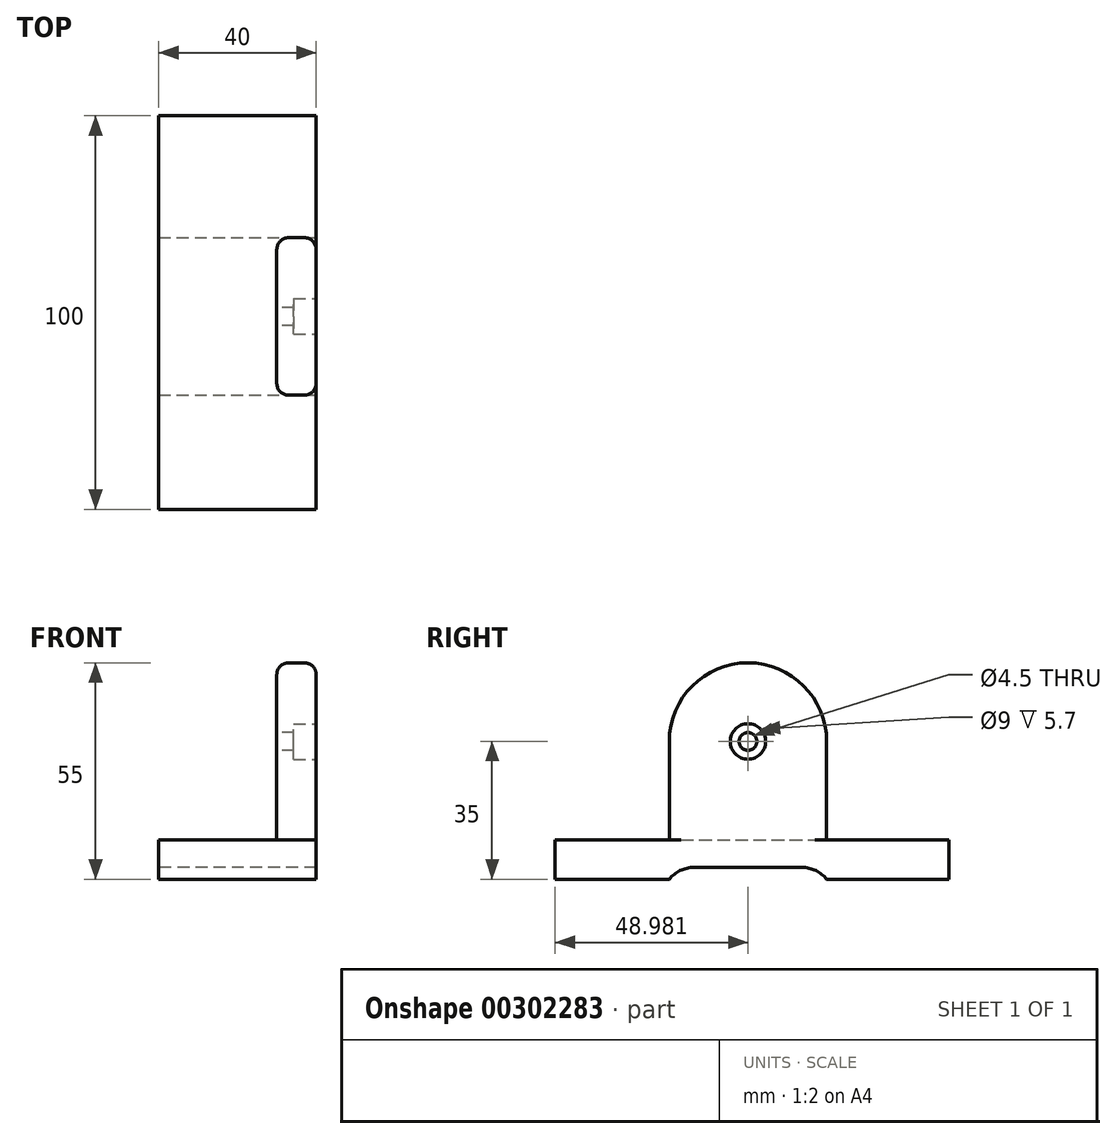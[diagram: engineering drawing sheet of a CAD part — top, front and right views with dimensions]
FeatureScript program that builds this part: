
annotation { "Feature Type Name" : "Feature", "Feature Type Description" : "" }
export const myFeature = defineFeature(function(context is Context, id is Id, definition is map)
    precondition{}
    {
        {
            var Q0;
            Q0=qCreatedBy(makeId("Top.planeOp"),FACE);
            var sketch = newSketch(context, id + "F0", { "sketchPlane" : qUnion([Q0])});
            skLineSegment(sketch, "E0.bottom", {"start": v(0, 0) * mm, "end": v(40, 0) * mm});
            skLineSegment(sketch, "E0.top", {"start": v(0, 100) * mm, "end": v(40, 100) * mm});
            skLineSegment(sketch, "E0.left", {"start": v(0, 0) * mm, "end": v(0, 100) * mm});
            skLineSegment(sketch, "E0.right", {"start": v(40, 0) * mm, "end": v(40, 100) * mm});
            skLineSegment(sketch, "E1.bottom", {"start": v(40.46, 100) * mm, "end": v(40, 100) * mm});
            skLineSegment(sketch, "E1.top", {"start": v(40.46, 96.76) * mm, "end": v(40, 96.76) * mm});
            skLineSegment(sketch, "E1.right", {"start": v(40, 100) * mm, "end": v(40, 96.76) * mm});
            skSolve(sketch);
        }
        {
            var Q0;
            Q0 = qSketchRegion(id + "F0", true);
            extrude(context, id + "F1", {"entities" : qUnion([Q0]), "depth" : 10 * mm});
        }
        {
            var Q0;
            Q0=makeQuery(id+"F1.opExtrude","SWEPT_FACE",FACE,{"disambiguationData":[OSD([sQuery(id+"F0.wireOp",EDGE,"E0.right"),sQuery(id+"F0.wireOp",EDGE,"E1.right")])]});
            var sketch = newSketch(context, id + "F2", { "sketchPlane" : qUnion([Q0])});
            skLineSegment(sketch, "E2", {"start": v(28.98, 0) * mm, "end": v(28.98, 35) * mm});
            skArc(sketch, "E3", {"start": v(28.98, 35) * mm, "mid": v(48.98, 55) * mm, "end": v(68.98, 35) * mm});
            skLineSegment(sketch, "E4", {"start": v(68.98, 35) * mm, "end": v(68.98, 0) * mm});
            skLineSegment(sketch, "E5", {"start": v(68.98, 0) * mm, "end": v(28.98, 0) * mm});
            skSolve(sketch);
        }
        {
            var Q0;
            Q0 = qSketchRegion(id + "F2", true);
            extrude(context, id + "F3", {"entities" : qUnion([Q0]), "operationType" : NewBodyOperationType.ADD, "oppositeDirection" : true, "depth" : 10 * mm});
        }
        {
            var Q0;
            Q0=makeQuery(id+"F3.opExtrude","CAP_FACE",FACE,{"disambiguationData":[OSD([sQuery(id+"F2.wireOp",EDGE,"E2"),sQuery(id+"F2.wireOp",EDGE,"E3"),sQuery(id+"F2.wireOp",EDGE,"E4"),sQuery(id+"F2.wireOp",EDGE,"E5")])],"isStart":false});
            var sketch = newSketch(context, id + "F4", { "sketchPlane" : qUnion([Q0])});
            skCircle(sketch, "E6", {"center": v(-48.98, 35) * mm, "radius": 2.25 * mm});
            skSolve(sketch);
        }
        {
            var Q0;
            Q0 = qSketchRegion(id + "F4", true);
            extrude(context, id + "F5", {"entities" : qUnion([Q0]), "operationType" : NewBodyOperationType.REMOVE, "endBound" : BoundingType.THROUGH_ALL, "oppositeDirection" : true, "depth" : 25 * mm});
        }
        {
            var Q0;
            Q0=makeQuery(id+"F3.boolean.opBoolean","MERGE",FACE,{"derivedFrom":[makeQuery(id+"F1.opExtrude","SWEPT_FACE",FACE,{"disambiguationData":[OSD([sQuery(id+"F0.wireOp",EDGE,"E0.right"),sQuery(id+"F0.wireOp",EDGE,"E1.right")])]}),makeQuery(id+"F3.opExtrude","CAP_FACE",FACE,{"disambiguationData":[OSD([sQuery(id+"F2.wireOp",EDGE,"E2"),sQuery(id+"F2.wireOp",EDGE,"E3"),sQuery(id+"F2.wireOp",EDGE,"E4"),sQuery(id+"F2.wireOp",EDGE,"E5")])],"isStart":true})]});
            var sketch = newSketch(context, id + "F6", { "sketchPlane" : qUnion([Q0])});
            skLineSegment(sketch, "E7.bottom", {"start": v(28.98, 0) * mm, "end": v(68.98, 0) * mm});
            skLineSegment(sketch, "E7.top", {"start": v(28.98, 3) * mm, "end": v(68.98, 3) * mm});
            skLineSegment(sketch, "E7.left", {"start": v(28.98, 0) * mm, "end": v(28.98, 3) * mm});
            skLineSegment(sketch, "E7.right", {"start": v(68.98, 0) * mm, "end": v(68.98, 3) * mm});
            skSolve(sketch);
        }
        {
            var Q0;
            Q0 = qSketchRegion(id + "F6", true);
            extrude(context, id + "F7", {"entities" : qUnion([Q0]), "operationType" : NewBodyOperationType.REMOVE, "endBound" : BoundingType.THROUGH_ALL, "oppositeDirection" : true, "depth" : 25 * mm});
        }
        {
            var Q0;
            Q0=makeQuery(id+"F3.boolean.opBoolean","MERGE",FACE,{"derivedFrom":[makeQuery(id+"F1.opExtrude","SWEPT_FACE",FACE,{"disambiguationData":[OSD([sQuery(id+"F0.wireOp",EDGE,"E0.right"),sQuery(id+"F0.wireOp",EDGE,"E1.right")])]}),makeQuery(id+"F3.opExtrude","CAP_FACE",FACE,{"disambiguationData":[OSD([sQuery(id+"F2.wireOp",EDGE,"E2"),sQuery(id+"F2.wireOp",EDGE,"E3"),sQuery(id+"F2.wireOp",EDGE,"E4"),sQuery(id+"F2.wireOp",EDGE,"E5")])],"isStart":true})]});
            var sketch = newSketch(context, id + "F8", { "sketchPlane" : qUnion([Q0])});
            skCircle(sketch, "E8", {"center": v(48.98, 35) * mm, "radius": 4.5 * mm});
            skSolve(sketch);
        }
        {
            var Q0;
            Q0 = qSketchRegion(id + "F8", true);
            extrude(context, id + "F9", {"entities" : qUnion([Q0]), "operationType" : NewBodyOperationType.REMOVE, "oppositeDirection" : true, "depth" : 5.7 * mm});
        }
        {
            var Q0;
            Q0=makeQuery(id+"F7.boolean.opBoolean","COPY",EDGE,{"derivedFrom":makeQuery(id+"F7.opExtrude","SWEPT_EDGE",EDGE,{"disambiguationData":[OSD([sQuery(id+"F6.wireOp",EDGE,"E7.top"),sQuery(id+"F6.wireOp",EDGE,"E7.right")])]})});
            var Q1;
            Q1=makeQuery(id+"F7.boolean.opBoolean","COPY",EDGE,{"derivedFrom":makeQuery(id+"F7.opExtrude","SWEPT_EDGE",EDGE,{"disambiguationData":[OSD([sQuery(id+"F6.wireOp",EDGE,"E7.top"),sQuery(id+"F6.wireOp",EDGE,"E7.left")])]})});
            fillet(context, id + "F10", {"entities" : qUnion([Q0, Q1]), "radius" : 8 * mm, "tangentPropagation" : true, "allowEdgeOverflow" : false});
        }
        {
            var Q0;
            Q0=makeQuery(id+"F3.opExtrude","CAP_EDGE",EDGE,{"disambiguationData":[OSD([sQuery(id+"F2.wireOp",EDGE,"E4")])],"isStart":true});
            var Q1;
            Q1=makeQuery(id+"F3.opExtrude","CAP_EDGE",EDGE,{"disambiguationData":[OSD([sQuery(id+"F2.wireOp",EDGE,"E4")])],"isStart":false});
            fillet(context, id + "F11", {"entities" : qUnion([Q0, Q1]), "radius" : 3 * mm, "tangentPropagation" : true, "allowEdgeOverflow" : false});
        }
    });
